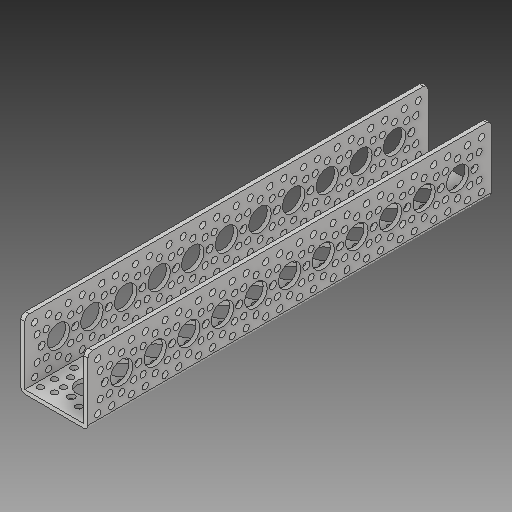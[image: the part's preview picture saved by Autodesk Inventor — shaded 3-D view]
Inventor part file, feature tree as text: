
AUTODESK INVENTOR PART (.ipt)
format: ipt  version: 2019 (Build 230136000, 136)  size: 600,064 bytes
history: native  units: in
note: dims shown in document units (in); Inventor stores cm internally (conversion verified against a paired STEP export)
features: fillet x1
ambient origin geometry x8: Origin, YZ Plane, XZ Plane, XY Plane, X Axis, Y Axis, Z Axis, Center Point
bodies: Solid1 (feature_tree)
feature tree (1):
  fillet  "Fillet1"  [1 undecoded]
note: 1 required parameter value undecoded (feature->parameter linkage not recoverable at this tier; creation-order binding heuristic only, values carry confidence <= 0.55)
